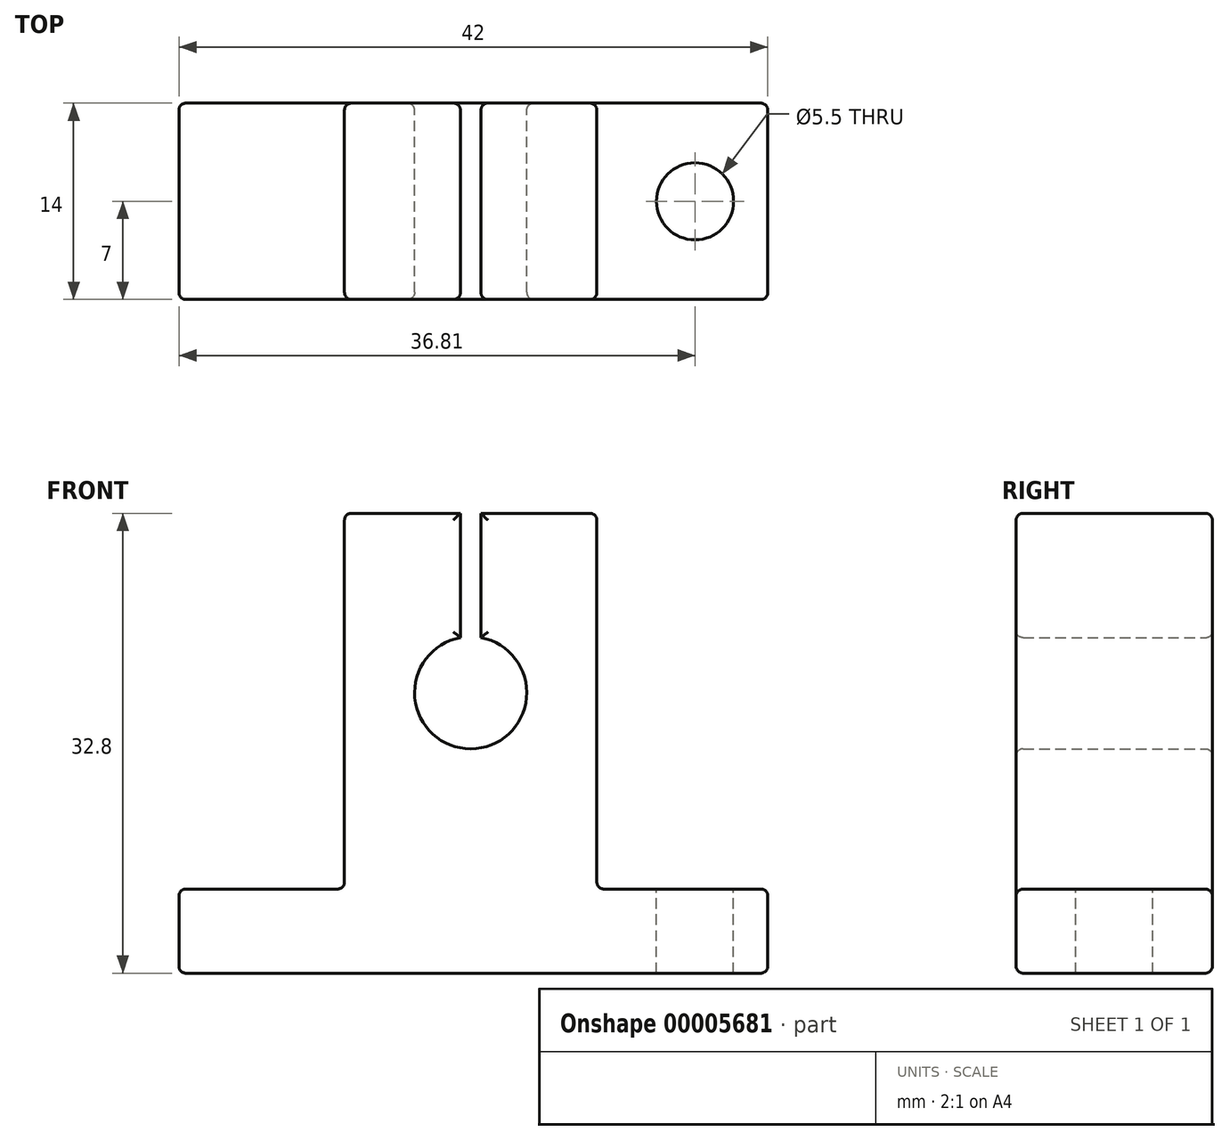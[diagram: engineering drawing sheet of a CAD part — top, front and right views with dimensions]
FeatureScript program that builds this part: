
annotation { "Feature Type Name" : "Feature", "Feature Type Description" : "" }
export const myFeature = defineFeature(function(context is Context, id is Id, definition is map)
    precondition{}
    {
        {
            var Q0;
            Q0=qCreatedBy(makeId("Front.planeOp"),FACE);
            var sketch = newSketch(context, id + "F0", { "sketchPlane" : qUnion([Q0])});
            skLineSegment(sketch, "E0.rect.top", {"start": v(9, 32.8) * mm, "end": v(0.73, 32.8) * mm});
            skLineSegment(sketch, "E0.rect.left", {"start": v(9, 6) * mm, "end": v(9, 32.8) * mm});
            skLineSegment(sketch, "E1.bottom", {"start": v(-20.8, 0) * mm, "end": v(21.2, 0) * mm});
            skLineSegment(sketch, "E1.top", {"start": v(-20.8, 6) * mm, "end": v(-9, 6) * mm});
            skLineSegment(sketch, "E1.left", {"start": v(-20.8, 0) * mm, "end": v(-20.8, 6) * mm});
            skLineSegment(sketch, "E1.right", {"start": v(21.2, 0) * mm, "end": v(21.2, 6) * mm});
            skArc(sketch, "E2", {"start": v(-0.73, 23.93) * mm, "mid": v(0, 16) * mm, "end": v(0.73, 23.93) * mm});
            skLineSegment(sketch, "E3", {"start": v(-9, 6) * mm, "end": v(-9, 32.8) * mm});
            skLineSegment(sketch, "E4", {"start": v(9, 6) * mm, "end": v(21.2, 6) * mm});
            skLineSegment(sketch, "E5", {"start": v(-0.73, 32.8) * mm, "end": v(-9, 32.8) * mm});
            skLineSegment(sketch, "E6", {"start": v(-0.73, 23.93) * mm, "end": v(-0.73, 32.8) * mm});
            skLineSegment(sketch, "E7", {"start": v(0.73, 23.93) * mm, "end": v(0.73, 32.8) * mm});
            skSolve(sketch);
        }
        {
            var Q0;
            Q0=makeQuery(id+"F0.imprint","IMPRINT",FACE,{"disambiguationData":[TD([[makeQuery(id+"F0.imprint","IMPRINT",EDGE,{"derivedFrom":sQuery(id+"F0.wireOp",EDGE,"E0.rect.top")}),1.0]])]});
            extrude(context, id + "F1", {"entities" : qUnion([Q0]), "depth" : 14 * mm, "symmetric" : true});
        }
        {
            var Q0;
            Q0=makeQuery(id+"F1.opExtrude","SWEPT_FACE",FACE,{"disambiguationData":[OSD([sQuery(id+"F0.wireOp",EDGE,"E4")])]});
            var sketch = newSketch(context, id + "F2", { "sketchPlane" : qUnion([Q0])});
            skCircle(sketch, "E8", {"center": v(16, 0) * mm, "radius": 2.75 * mm});
            skCircle(sketch, "E9.0.MirrorC", {"center": v(-16, 0) * mm, "radius": 2.75 * mm});
            skSolve(sketch);
        }
        {
            var Q0;
            Q0=makeQuery(id+"F2.imprint","IMPRINT",FACE,{"disambiguationData":[TD([[makeQuery(id+"F2.imprint","IMPRINT",EDGE,{"derivedFrom":sQuery(id+"F2.wireOp",EDGE,"E9.0.MirrorC")}),-1.0]])]});
            var Q1;
            Q1=makeQuery(id+"F2.imprint","IMPRINT",FACE,{"disambiguationData":[TD([[makeQuery(id+"F2.imprint","IMPRINT",EDGE,{"derivedFrom":sQuery(id+"F2.wireOp",EDGE,"E8")}),1.0]])]});
            extrude(context, id + "F3", {"entities" : qUnion([Q0, Q1]), "operationType" : NewBodyOperationType.REMOVE, "endBound" : BoundingType.THROUGH_ALL, "oppositeDirection" : true, "depth" : 16.58 * mm});
        }
        {
            var Q0;
            Q0=makeQuery(id+"F1.opExtrude","CAP_FACE",FACE,{"disambiguationData":[OSD([sQuery(id+"F0.wireOp",EDGE,"E0.rect.top"),sQuery(id+"F0.wireOp",EDGE,"E0.rect.left"),sQuery(id+"F0.wireOp",EDGE,"E1.bottom"),sQuery(id+"F0.wireOp",EDGE,"E1.top"),sQuery(id+"F0.wireOp",EDGE,"E1.left"),sQuery(id+"F0.wireOp",EDGE,"E1.right"),sQuery(id+"F0.wireOp",EDGE,"E2"),sQuery(id+"F0.wireOp",EDGE,"E3"),sQuery(id+"F0.wireOp",EDGE,"E4"),sQuery(id+"F0.wireOp",EDGE,"E5"),sQuery(id+"F0.wireOp",EDGE,"E6"),sQuery(id+"F0.wireOp",EDGE,"E7")])],"isStart":false});
            var Q1;
            Q1=makeQuery(id+"F1.opExtrude","CAP_FACE",FACE,{"disambiguationData":[OSD([sQuery(id+"F0.wireOp",EDGE,"E0.rect.top"),sQuery(id+"F0.wireOp",EDGE,"E0.rect.left"),sQuery(id+"F0.wireOp",EDGE,"E1.bottom"),sQuery(id+"F0.wireOp",EDGE,"E1.top"),sQuery(id+"F0.wireOp",EDGE,"E1.left"),sQuery(id+"F0.wireOp",EDGE,"E1.right"),sQuery(id+"F0.wireOp",EDGE,"E2"),sQuery(id+"F0.wireOp",EDGE,"E3"),sQuery(id+"F0.wireOp",EDGE,"E4"),sQuery(id+"F0.wireOp",EDGE,"E5"),sQuery(id+"F0.wireOp",EDGE,"E6"),sQuery(id+"F0.wireOp",EDGE,"E7")])],"isStart":true});
            var Q2;
            Q2=makeQuery(id+"F1.opExtrude","SWEPT_FACE",FACE,{"disambiguationData":[OSD([sQuery(id+"F0.wireOp",EDGE,"E0.rect.left")])]});
            var Q3;
            Q3=makeQuery(id+"F1.opExtrude","SWEPT_FACE",FACE,{"disambiguationData":[OSD([sQuery(id+"F0.wireOp",EDGE,"E1.right")])]});
            var Q4;
            Q4=makeQuery(id+"F1.opExtrude","SWEPT_FACE",FACE,{"disambiguationData":[OSD([sQuery(id+"F0.wireOp",EDGE,"E3")])]});
            var Q5;
            Q5=makeQuery(id+"F1.opExtrude","SWEPT_FACE",FACE,{"disambiguationData":[OSD([sQuery(id+"F0.wireOp",EDGE,"E1.left")])]});
            fillet(context, id + "F4", {"entities" : qUnion([Q0, Q1, Q2, Q3, Q4, Q5]), "radius" : 0.5 * mm, "tangentPropagation" : true, "allowEdgeOverflow" : false});
        }
    });
